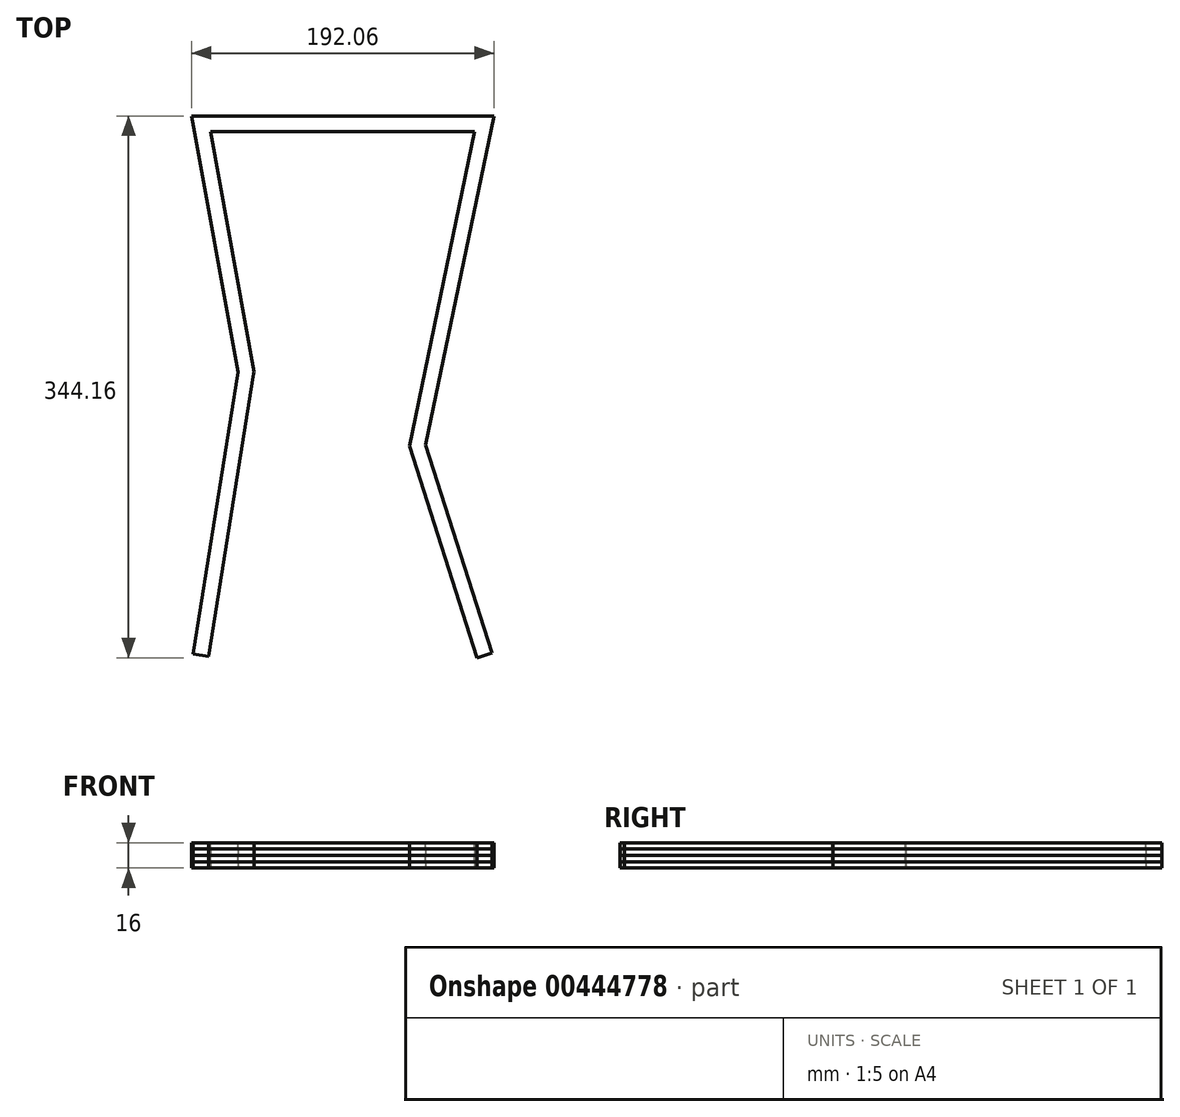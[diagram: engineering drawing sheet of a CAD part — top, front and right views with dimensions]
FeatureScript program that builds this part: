
annotation { "Feature Type Name" : "Feature", "Feature Type Description" : "" }
export const myFeature = defineFeature(function(context is Context, id is Id, definition is map)
    precondition{}
    {
        {
            var Q0;
            Q0=qCreatedBy(makeId("Top.planeOp"),FACE);
            var sketch = newSketch(context, id + "F0", { "sketchPlane" : qUnion([Q0])});
            skLineSegment(sketch, "E0", {"start": v(85.12, -172.08) * mm, "end": v(42.4, -37.47) * mm});
            skLineSegment(sketch, "E1", {"start": v(42.4, -37.47) * mm, "end": v(83.75, 162.08) * mm});
            skLineSegment(sketch, "E2", {"start": v(83.75, 162.08) * mm, "end": v(-84.06, 162.08) * mm});
            skLineSegment(sketch, "E3", {"start": v(-84.06, 162.08) * mm, "end": v(-56.4, 9.43) * mm});
            skLineSegment(sketch, "E4", {"start": v(-56.4, 9.43) * mm, "end": v(-56.53, 8.59) * mm});
            skLineSegment(sketch, "E5", {"start": v(-56.53, 8.59) * mm, "end": v(-85.1, -171.35) * mm});
            skLineSegment(sketch, "E6", {"start": v(-85.1, -171.35) * mm, "end": v(-94.98, -169.78) * mm});
            skLineSegment(sketch, "E7", {"start": v(-94.98, -169.78) * mm, "end": v(-66.54, 9.31) * mm});
            skLineSegment(sketch, "E8", {"start": v(-66.54, 9.31) * mm, "end": v(-96.03, 172.08) * mm});
            skLineSegment(sketch, "E9", {"start": v(-96.03, 172.08) * mm, "end": v(96.03, 172.08) * mm});
            skLineSegment(sketch, "E10", {"start": v(96.03, 172.08) * mm, "end": v(52.71, -36.94) * mm});
            skLineSegment(sketch, "E11", {"start": v(52.71, -36.94) * mm, "end": v(94.66, -169.05) * mm});
            skLineSegment(sketch, "E12", {"start": v(94.66, -169.05) * mm, "end": v(85.12, -172.08) * mm});
            skSolve(sketch);
        }
        {
            var Q0;
            Q0 = qSketchRegion(id + "F0", true);
            extrude(context, id + "F1", {"entities" : qUnion([Q0]), "depth" : 4 * mm});
        }
        {
            var Q0;
            Q0=makeQuery(id+"F1.opExtrude","SWEPT_BODY",BODY,{"disambiguationData":[OSD([sQuery(id+"F0.wireOp",EDGE,"E0"),sQuery(id+"F0.wireOp",EDGE,"E1"),sQuery(id+"F0.wireOp",EDGE,"E2"),sQuery(id+"F0.wireOp",EDGE,"E3"),sQuery(id+"F0.wireOp",EDGE,"E4"),sQuery(id+"F0.wireOp",EDGE,"E5"),sQuery(id+"F0.wireOp",EDGE,"E6"),sQuery(id+"F0.wireOp",EDGE,"E7"),sQuery(id+"F0.wireOp",EDGE,"E8"),sQuery(id+"F0.wireOp",EDGE,"E9"),sQuery(id+"F0.wireOp",EDGE,"E10"),sQuery(id+"F0.wireOp",EDGE,"E11"),sQuery(id+"F0.wireOp",EDGE,"E12")])]});
            var Q1;
            Q1=makeQuery(id+"F1.opExtrude","CAP_FACE",FACE,{"disambiguationData":[OSD([sQuery(id+"F0.wireOp",EDGE,"E0"),sQuery(id+"F0.wireOp",EDGE,"E1"),sQuery(id+"F0.wireOp",EDGE,"E2"),sQuery(id+"F0.wireOp",EDGE,"E3"),sQuery(id+"F0.wireOp",EDGE,"E4"),sQuery(id+"F0.wireOp",EDGE,"E5"),sQuery(id+"F0.wireOp",EDGE,"E6"),sQuery(id+"F0.wireOp",EDGE,"E7"),sQuery(id+"F0.wireOp",EDGE,"E8"),sQuery(id+"F0.wireOp",EDGE,"E9"),sQuery(id+"F0.wireOp",EDGE,"E10"),sQuery(id+"F0.wireOp",EDGE,"E11"),sQuery(id+"F0.wireOp",EDGE,"E12")])],"isStart":false});
            mirror(context, id + "F2", {"entities" : qUnion([Q0]), "mirrorPlane" : qUnion([Q1])});
        }
        {
            var Q0;
            Q0=makeQuery(id+"F2.opPattern","COPY",BODY,{"derivedFrom":makeQuery(id+"F1.opExtrude","SWEPT_BODY",BODY,{"disambiguationData":[OSD([sQuery(id+"F0.wireOp",EDGE,"E0"),sQuery(id+"F0.wireOp",EDGE,"E1"),sQuery(id+"F0.wireOp",EDGE,"E2"),sQuery(id+"F0.wireOp",EDGE,"E3"),sQuery(id+"F0.wireOp",EDGE,"E4"),sQuery(id+"F0.wireOp",EDGE,"E5"),sQuery(id+"F0.wireOp",EDGE,"E6"),sQuery(id+"F0.wireOp",EDGE,"E7"),sQuery(id+"F0.wireOp",EDGE,"E8"),sQuery(id+"F0.wireOp",EDGE,"E9"),sQuery(id+"F0.wireOp",EDGE,"E10"),sQuery(id+"F0.wireOp",EDGE,"E11"),sQuery(id+"F0.wireOp",EDGE,"E12")])]}),"instanceName":"1"});
            var Q1;
            Q1=makeQuery(id+"F1.opExtrude","SWEPT_BODY",BODY,{"disambiguationData":[OSD([sQuery(id+"F0.wireOp",EDGE,"E0"),sQuery(id+"F0.wireOp",EDGE,"E1"),sQuery(id+"F0.wireOp",EDGE,"E2"),sQuery(id+"F0.wireOp",EDGE,"E3"),sQuery(id+"F0.wireOp",EDGE,"E4"),sQuery(id+"F0.wireOp",EDGE,"E5"),sQuery(id+"F0.wireOp",EDGE,"E6"),sQuery(id+"F0.wireOp",EDGE,"E7"),sQuery(id+"F0.wireOp",EDGE,"E8"),sQuery(id+"F0.wireOp",EDGE,"E9"),sQuery(id+"F0.wireOp",EDGE,"E10"),sQuery(id+"F0.wireOp",EDGE,"E11"),sQuery(id+"F0.wireOp",EDGE,"E12")])]});
            var Q2;
            Q2=makeQuery(id+"F2.opPattern","COPY",FACE,{"derivedFrom":makeQuery(id+"F1.opExtrude","CAP_FACE",FACE,{"disambiguationData":[OSD([sQuery(id+"F0.wireOp",EDGE,"E0"),sQuery(id+"F0.wireOp",EDGE,"E1"),sQuery(id+"F0.wireOp",EDGE,"E2"),sQuery(id+"F0.wireOp",EDGE,"E3"),sQuery(id+"F0.wireOp",EDGE,"E4"),sQuery(id+"F0.wireOp",EDGE,"E5"),sQuery(id+"F0.wireOp",EDGE,"E6"),sQuery(id+"F0.wireOp",EDGE,"E7"),sQuery(id+"F0.wireOp",EDGE,"E8"),sQuery(id+"F0.wireOp",EDGE,"E9"),sQuery(id+"F0.wireOp",EDGE,"E10"),sQuery(id+"F0.wireOp",EDGE,"E11"),sQuery(id+"F0.wireOp",EDGE,"E12")])],"isStart":true}),"instanceName":"1"});
            mirror(context, id + "F3", {"entities" : qUnion([Q0, Q1]), "mirrorPlane" : qUnion([Q2])});
        }
    });
